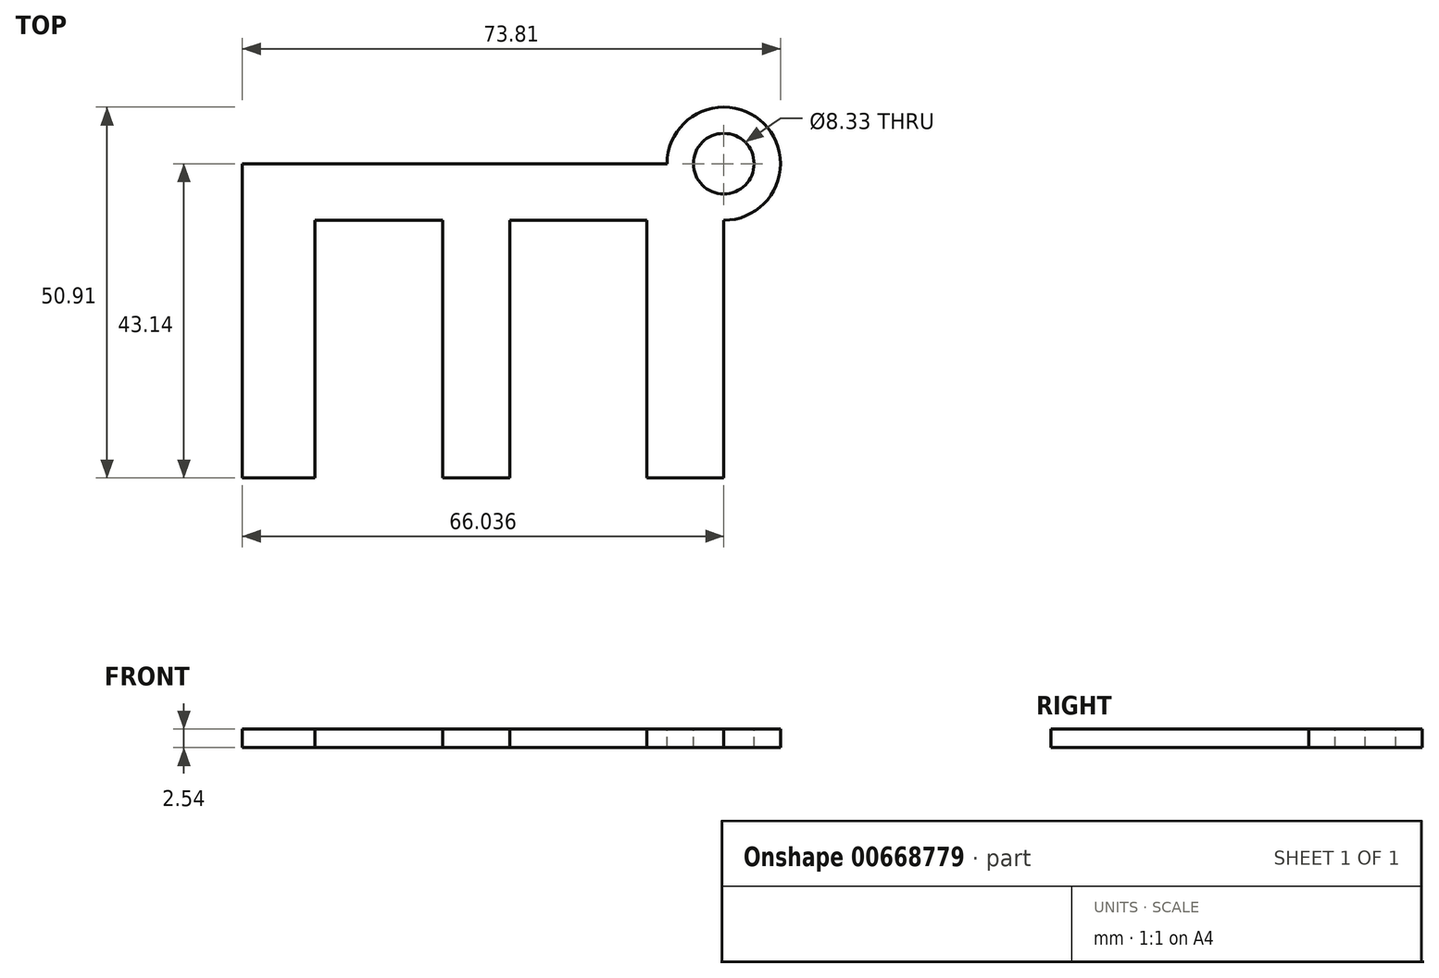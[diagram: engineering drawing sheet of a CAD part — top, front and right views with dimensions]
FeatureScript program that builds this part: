
annotation { "Feature Type Name" : "Feature", "Feature Type Description" : "" }
export const myFeature = defineFeature(function(context is Context, id is Id, definition is map)
    precondition{}
    {
        {
            var Q0;
            Q0=qCreatedBy(makeId("Top.planeOp"),FACE);
            var sketch = newSketch(context, id + "F0", { "sketchPlane" : qUnion([Q0])});
            skLineSegment(sketch, "E0.bottom", {"start": v(-33.86, 21.23) * mm, "end": v(32.18, 21.23) * mm});
            skLineSegment(sketch, "E0.top", {"start": v(-33.86, -21.9) * mm, "end": v(32.18, -21.9) * mm});
            skLineSegment(sketch, "E0.left", {"start": v(-33.86, 21.23) * mm, "end": v(-33.86, -21.9) * mm});
            skLineSegment(sketch, "E0.right", {"start": v(32.18, 21.23) * mm, "end": v(32.18, -21.9) * mm});
            skSolve(sketch);
        }
        {
            var Q0;
            Q0=makeQuery(id+"F0.imprint","IMPRINT",FACE,{"disambiguationData":[TD([[makeQuery(id+"F0.imprint","IMPRINT",EDGE,{"derivedFrom":sQuery(id+"F0.wireOp",EDGE,"E0.bottom")}),-1.0]])]});
            extrude(context, id + "F1", {"entities" : qUnion([Q0]), "depth" : 2.54 * mm, "offsetDistance" : 25.4 * mm});
        }
        {
            var Q0;
            Q0=makeQuery(id+"F1.opExtrude","CAP_FACE",FACE,{"disambiguationData":[OSD([sQuery(id+"F0.wireOp",EDGE,"E0.bottom"),sQuery(id+"F0.wireOp",EDGE,"E0.top"),sQuery(id+"F0.wireOp",EDGE,"E0.left"),sQuery(id+"F0.wireOp",EDGE,"E0.right")])],"isStart":false});
            var sketch = newSketch(context, id + "F2", { "sketchPlane" : qUnion([Q0])});
            skLineSegment(sketch, "E1.bottom", {"start": v(2.86, 13.46) * mm, "end": v(21.65, 13.46) * mm});
            skLineSegment(sketch, "E1.top", {"start": v(2.86, -21.9) * mm, "end": v(21.65, -21.9) * mm});
            skLineSegment(sketch, "E1.left", {"start": v(2.86, 13.46) * mm, "end": v(2.86, -21.9) * mm});
            skLineSegment(sketch, "E1.right", {"start": v(21.65, 13.46) * mm, "end": v(21.65, -21.9) * mm});
            skSolve(sketch);
        }
        {
            var Q0;
            Q0 = qSketchRegion(id + "F2", true);
            extrude(context, id + "F3", {"entities" : qUnion([Q0]), "operationType" : NewBodyOperationType.REMOVE, "oppositeDirection" : true, "depth" : 25.4 * mm, "offsetDistance" : 25.4 * mm});
        }
        {
            var Q0;
            Q0=makeQuery(id+"F1.opExtrude","CAP_FACE",FACE,{"disambiguationData":[OSD([sQuery(id+"F0.wireOp",EDGE,"E0.bottom"),sQuery(id+"F0.wireOp",EDGE,"E0.top"),sQuery(id+"F0.wireOp",EDGE,"E0.left"),sQuery(id+"F0.wireOp",EDGE,"E0.right")])],"isStart":false});
            var sketch = newSketch(context, id + "F4", { "sketchPlane" : qUnion([Q0])});
            skLineSegment(sketch, "E2.bottom", {"start": v(-6.38, 13.46) * mm, "end": v(-23.91, 13.46) * mm});
            skLineSegment(sketch, "E2.top", {"start": v(-6.38, -21.9) * mm, "end": v(-23.91, -21.9) * mm});
            skLineSegment(sketch, "E2.left", {"start": v(-6.38, 13.46) * mm, "end": v(-6.38, -21.9) * mm});
            skLineSegment(sketch, "E2.right", {"start": v(-23.91, 13.46) * mm, "end": v(-23.91, -21.9) * mm});
            skSolve(sketch);
        }
        {
            var Q0;
            Q0 = qSketchRegion(id + "F4", true);
            extrude(context, id + "F5", {"entities" : qUnion([Q0]), "operationType" : NewBodyOperationType.REMOVE, "oppositeDirection" : true, "depth" : 25.4 * mm, "offsetDistance" : 25.4 * mm});
        }
        {
            var Q0;
            Q0=makeQuery(id+"F1.opExtrude","CAP_FACE",FACE,{"disambiguationData":[OSD([sQuery(id+"F0.wireOp",EDGE,"E0.bottom"),sQuery(id+"F0.wireOp",EDGE,"E0.top"),sQuery(id+"F0.wireOp",EDGE,"E0.left"),sQuery(id+"F0.wireOp",EDGE,"E0.right")])],"isStart":false});
            var sketch = newSketch(context, id + "F6", { "sketchPlane" : qUnion([Q0])});
            skCircle(sketch, "E3", {"center": v(32.18, 21.23) * mm, "radius": 7.77 * mm});
            skSolve(sketch);
        }
        {
            var Q0;
            Q0 = qSketchRegion(id + "F6", true);
            extrude(context, id + "F7", {"entities" : qUnion([Q0]), "operationType" : NewBodyOperationType.ADD, "depth" : -2.54 * mm, "offsetDistance" : 25.4 * mm});
        }
        {
            var Q0;
            Q0=makeQuery(id+"F7.boolean.opBoolean","MERGE",FACE,{"derivedFrom":[makeQuery(id+"F1.opExtrude","CAP_FACE",FACE,{"disambiguationData":[OSD([sQuery(id+"F0.wireOp",EDGE,"E0.bottom"),sQuery(id+"F0.wireOp",EDGE,"E0.top"),sQuery(id+"F0.wireOp",EDGE,"E0.left"),sQuery(id+"F0.wireOp",EDGE,"E0.right")])],"isStart":false}),makeQuery(id+"F7.opExtrude","CAP_FACE",FACE,{"disambiguationData":[OSD([sQuery(id+"F6.wireOp",EDGE,"E3")])],"isStart":true})]});
            var sketch = newSketch(context, id + "F8", { "sketchPlane" : qUnion([Q0])});
            skCircle(sketch, "E4", {"center": v(32.18, 21.23) * mm, "radius": 4.16 * mm});
            skSolve(sketch);
        }
        {
            var Q0;
            Q0 = qSketchRegion(id + "F8", true);
            extrude(context, id + "F9", {"entities" : qUnion([Q0]), "operationType" : NewBodyOperationType.REMOVE, "oppositeDirection" : true, "depth" : 25.4 * mm, "offsetDistance" : 25.4 * mm});
        }
    });
